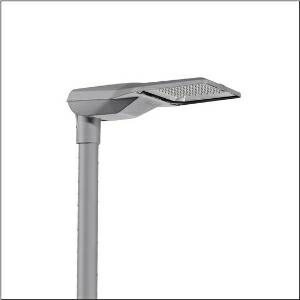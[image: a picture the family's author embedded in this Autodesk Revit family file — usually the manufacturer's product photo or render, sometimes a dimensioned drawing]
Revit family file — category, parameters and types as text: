
# Revit family: streetlight_sl_21_iq_midi___p0_5a_5xe3v31g08nb_569c
name_source: partatom
category: Lighting Fixtures
units: mm (PartAtom-declared; Revit-internal decimal feet)

## family parameters
Cut with Voids When Loaded = No
Host = Face
Light Source = No
Part Type = Normal
Room Calculation Point = No
Round Connector Dimension = Use Diameter
Shared = No

## types (1)
- --- (1 x LED, 22830 lm, 155.5 W, 3000K)
    Apparent Load = 155 VA
    CIE Flux Codes = 37 73 96 100 100
    Color Rendering = 70
    Color Temperature = 3000K
    Default Elevation = 1800 mm
    Description = Streetlight SL 21 iQ midi, mast luminaire, primary light control with lens, of PMMA, primary optical cover: cover, of toughened safety glass, transparent, light distribution: P0.5a, light emission: direct distribution, primary light characteristic: asymmetric, installation type: post-top, side-entry, LED, High Power LED, rated luminous flux: 22.830lm, luminous efficacy: 147lm/W, light colour: 730, colour temperature: 3000K, control gear: iQ Street-Remote, control: pre-setting: linear dimming characteristic, Street-Remote, Auto-Match, Temp-Guard, Lumen-Switch, Night-Set, Smart-Wire, Light-Fading, Desk-Remote (wireless, voltage-free reading and setting of iQ features in the workshop via application-optimized NFC function/RFID function), optimised constant luminous flux control (CLO 2.0), mains connection: 230..240V, AC, 50/60Hz, start of lifetime: 156W, end of service life: 162W, reduction: 69W, luminaire housing, of diecast aluminium, powder-coated, SITECO metallic grey (DB 702S), corrosivity category C5 high according to DIN EN ISO 12944, please order mast flange separately, inclination adjustable: 0°, 5°, 10°, 15°, sealing non-destructively replaceable, multi-level sealing system, length: 644mm, width: 335mm, height: 110mm, mast flange for spigot size: 42mm (side-entry): 5XC10008XM4, 60/48mm (side-entry/post-top): 5XC10108XM2, 76/60mm (side-entry/post-top): 5XC10108XM1, mounting height: 4..8m, protection rating (complete): IP66, insulation class (complete): insulation class II (safety insulation), certification: CE, ENEC, ENEC+, VDE, impact resistance: IK10, permissible operating ambient temperature for outdoor applications: -40..+50°C, standard-compliant lighting for roads and squares, packaging unit: 1 piece

Light Distribution: P0.5a
    Height = 111 mm
    Lamp = 1 x LED
    Lamp Light Flux = 22830 lm
    Lamp Power = 155.5 W
    Lamp count = 1
    Length = 644 mm
    Luminous efficacy = 147 lm/W
    Manufacturer = Siteco
    ModVariant = No
    Model = 5XE3V31G08NB
    Number of Poles = 1
    OnlyDefault = Yes
    Power Factor = 1
    Product Name = Streetlight SL 21 iQ midi | P0.5a
    Product group = mast luminaire | pylon top
    ProductGroupID = 6100
    Protection Class = Protection class II
    Protection Degree = IP 66
    RLX_Detail_Level = 1
    RLX_Emergency_Light_Flux = 0 lm
    RLX_Emergency_Type = 0
    RLX_Emergency_Type_DB = No
    RlxData = <blob elided: 91037 chars, md5=b29f2fd5>
    Socket = socket
    Standby Power = 0 W
    System Light Flux = 22831 lm
    System Power = 155 W
    Type Comments = factory setting: luminous flux: 100 % | dim-lin: 254 | 823 mA
    Type Image = l_1004298.jpg
    URL = http://relux.com
    VarID = @adj_076859
    Voltage = 0 V
    Weight = 0.00 kg
    Width = 336 mm

## geometry (parser evidence)
native form markers: Blend x4, Sweep x11
no freeform markers — native parametric forms only
